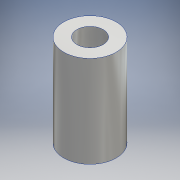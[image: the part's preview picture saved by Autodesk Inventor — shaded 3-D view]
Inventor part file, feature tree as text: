
AUTODESK INVENTOR PART (.ipt)
format: ipt  version: 2016 (Build 200138000, 138)  size: 96,256 bytes
history: native  units: mm
features: other x1, extrude x1, sketch x1
ambient origin geometry x8: Origin, YZ Plane, XZ Plane, XY Plane, X Axis, Y Axis, Z Axis, Center Point
bodies: Body1 (feature_tree)
feature tree (3):
  other  "ソリッド1"
  extrude  "押し出し1"  Depth=8.0mm
  sketch  "スケッチ1"
